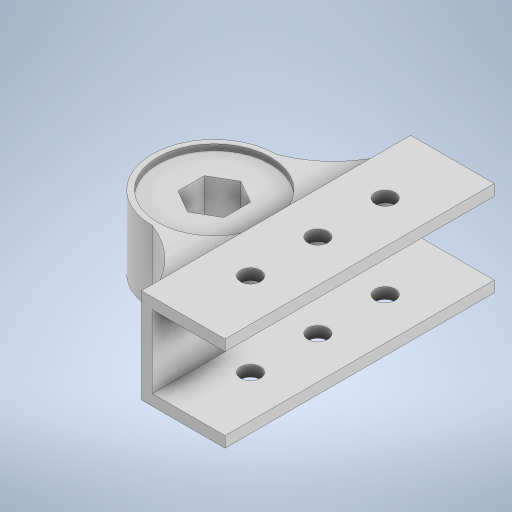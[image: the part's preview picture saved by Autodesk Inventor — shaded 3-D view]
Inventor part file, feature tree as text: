
AUTODESK INVENTOR PART (.ipt)
format: ipt  version: 2023.1 (Build 271208000, 208)  size: 325,120 bytes
history: native  units: in
note: dims shown in document units (in); Inventor stores cm internally (conversion verified against a paired STEP export)
features: sketch x11, extrude x9, hole x2
ambient origin geometry x8: Origin, YZ Plane, XZ Plane, XY Plane, X Axis, Y Axis, Z Axis, Center Point
bodies: Solid1 (feature_tree)
feature tree (22):
  extrude  "Extrusion1"  Depth=0.7866in TaperAngle=0.0deg
  extrude  "Extrusion2"  Depth=0.0634in TaperAngle=0.0deg
  extrude  "Extrusion4"  Depth=0.0634in TaperAngle=0.0deg
  extrude  "Extrusion5"  Depth=0.7874in
  extrude  "Extrusion6"  Depth=0.7866in TaperAngle=0.0deg
  extrude  "Extrusion7"  Depth=0.1181in TaperAngle=0.0deg
  extrude  "Extrusion8"  Depth=0.1181in
  extrude  "Extrusion9"  Depth=0.1181in
  extrude  "Extrusion10"  TaperAngle=0.0deg  [1 undecoded]
  hole  "Hole1"  [1 undecoded]
  hole  "Hole2"  [1 undecoded]
  sketch  "Sketch1"  dims[d6=1.3386in d7=0.7866in d8=0.0in]
  sketch  "Sketch2"  dims[d9=1.2205in d10=0.0634in d11=0.0in]
  sketch  "Sketch4"  dims[d15=1.2205in d16=0.0634in d17=0.0in]
  sketch  "Sketch5"  dims[d18=0.7874in d19=0.7874in]
  sketch  "Sketch7"  dims[d20=0.7874in d21=0.7866in d22=0.0in]
  sketch  "Sketch9"  dims[d23=0.1181in d24=0.0in d25=0.1181in d26=0.0in]
  sketch  "Sketch11"  dims[d27=0.1181in d28=0.0in d29=0.1181in]
  sketch  "Sketch12"  dims[d30=0.1181in d31=0.1181in]
  sketch  "Sketch13"  dims[d32=0.0in d33=0.0in d35=0.0in d36=0.0in]
  sketch  "Sketch14"  dims[d37=0.4528in d38=1.4567in]
  sketch  "Sketch15"  dims[d39=0.2165in d40=0.2362in d41=0.4094in d42=0.0787in d43=90.0deg d44=0.315in d45=0.8108in d47=0.7283in d48=0.7283in d49=0.2165in d50=0.2362in d51=0.1575in d52=0.0787in d53=90.0deg d54=0.315in d55=0.8108in]
note: 3 required parameter values undecoded (feature->parameter linkage not recoverable at this tier; creation-order binding heuristic only, values carry confidence <= 0.55)
